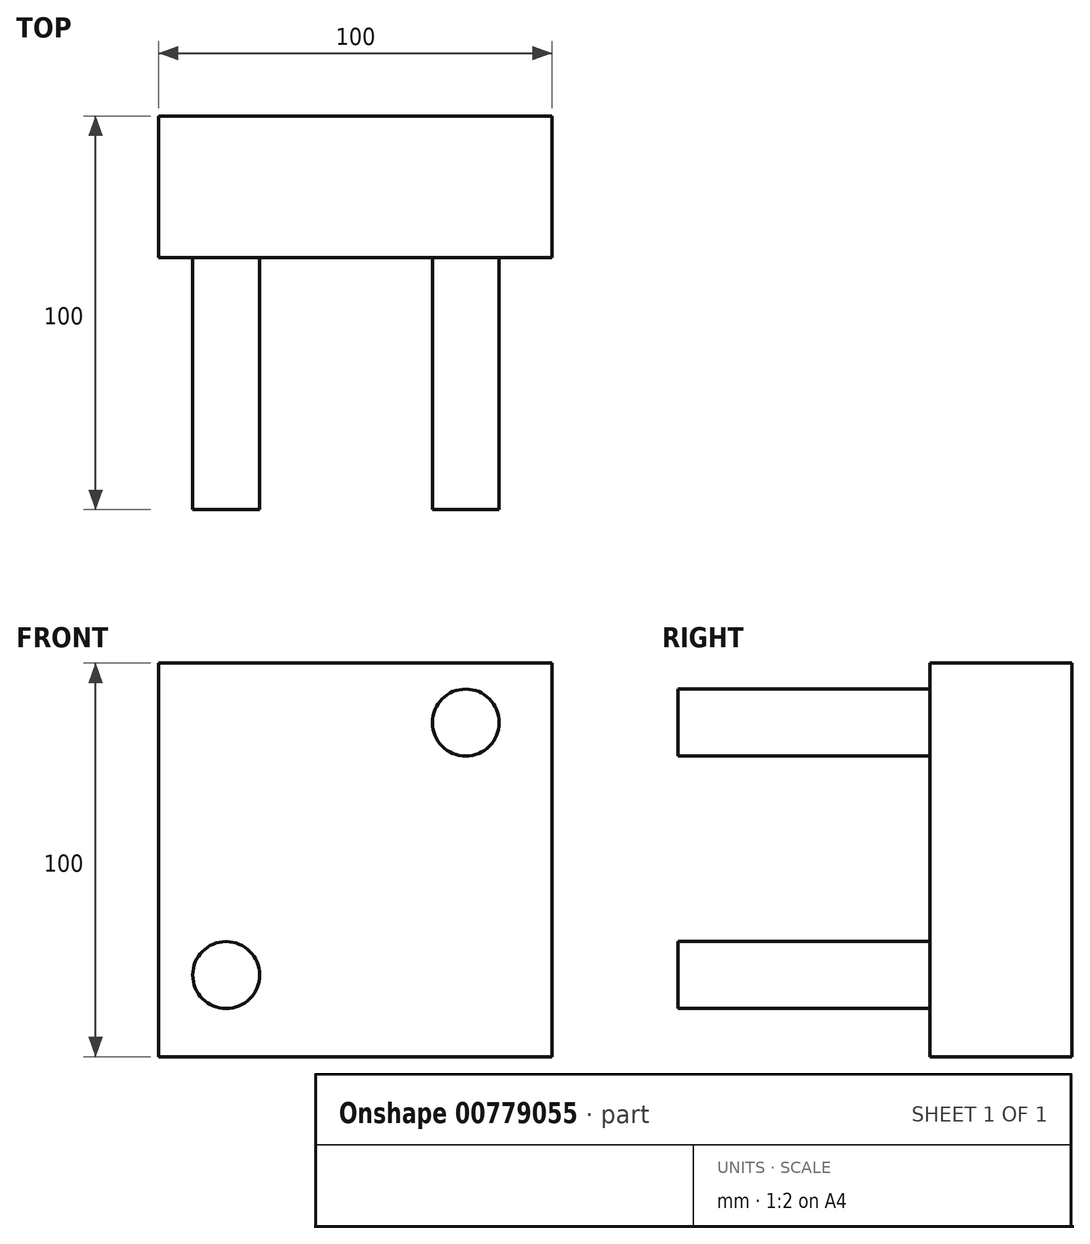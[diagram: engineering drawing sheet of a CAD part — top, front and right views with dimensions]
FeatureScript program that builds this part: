
annotation { "Feature Type Name" : "Feature", "Feature Type Description" : "" }
export const myFeature = defineFeature(function(context is Context, id is Id, definition is map)
    precondition{}
    {
        {
            var Q0;
            Q0=qCreatedBy(makeId("Front.planeOp"),FACE);
            var sketch = newSketch(context, id + "F0", { "sketchPlane" : qUnion([Q0])});
            skLineSegment(sketch, "E0.bottom", {"start": v(-47.6, 63.6) * mm, "end": v(52.4, 63.6) * mm});
            skLineSegment(sketch, "E0.top", {"start": v(-47.6, -36.4) * mm, "end": v(52.4, -36.4) * mm});
            skLineSegment(sketch, "E0.left", {"start": v(-47.6, 63.6) * mm, "end": v(-47.6, -36.4) * mm});
            skLineSegment(sketch, "E0.right", {"start": v(52.4, 63.6) * mm, "end": v(52.4, -36.4) * mm});
            skSolve(sketch);
        }
        {
            var Q0;
            Q0 = qSketchRegion(id + "F0", true);
            extrude(context, id + "F1", {"entities" : qUnion([Q0]), "depth" : 100 * mm, "offsetDistance" : 25 * mm});
        }
        {
            var Q0;
            Q0=makeQuery(id+"F1.opExtrude","CAP_FACE",FACE,{"disambiguationData":[OSD([sQuery(id+"F0.wireOp",EDGE,"E0.bottom"),sQuery(id+"F0.wireOp",EDGE,"E0.top"),sQuery(id+"F0.wireOp",EDGE,"E0.left"),sQuery(id+"F0.wireOp",EDGE,"E0.right")])],"isStart":false});
            var sketch = newSketch(context, id + "F2", { "sketchPlane" : qUnion([Q0])});
            skCircle(sketch, "E1", {"center": v(-30.44, 48.5) * mm, "radius": 8.5 * mm});
            skCircle(sketch, "E2.MirrorC", {"center": v(30.44, 48.5) * mm, "radius": 8.5 * mm});
            skCircle(sketch, "E3.MirrorC", {"center": v(-30.44, -15.65) * mm, "radius": 8.5 * mm});
            skCircle(sketch, "E4.MirrorC", {"center": v(30.44, -15.65) * mm, "radius": 8.5 * mm});
            skSolve(sketch);
        }
        {
            var Q0;
            Q0=makeQuery(id+"F2.imprint","IMPRINT",FACE,{"disambiguationData":[TD([[makeQuery(id+"F2.imprint","IMPRINT",EDGE,{"derivedFrom":sQuery(id+"F2.wireOp",EDGE,"E2.MirrorC")}),-1.0]])]});
            var Q1;
            Q1=makeQuery(id+"F2.imprint","IMPRINT",FACE,{"disambiguationData":[TD([[makeQuery(id+"F2.imprint","IMPRINT",EDGE,{"derivedFrom":sQuery(id+"F2.wireOp",EDGE,"E3.MirrorC")}),-1.0]])]});
            var Q2;
            Q2=makeQuery(id+"F2.imprint","IMPRINT",FACE,{"disambiguationData":[TD([[makeQuery(id+"F2.imprint","IMPRINT",EDGE,{"derivedFrom":sQuery(id+"F2.wireOp",EDGE,"E4.MirrorC")}),1.0]])]});
            var Q3;
            Q3=makeQuery(id+"F2.imprint","IMPRINT",FACE,{"disambiguationData":[TD([[makeQuery(id+"F2.imprint","IMPRINT",EDGE,{"derivedFrom":sQuery(id+"F2.wireOp",EDGE,"f4eeDJDL-5iWv-AFPj-o37r-ou3OiQOnMEaG")}),1.0]])]});
            var Q4;
            Q4=makeQuery(id+"F2.imprint","IMPRINT",FACE,{"disambiguationData":[TD([[makeQuery(id+"F2.imprint","IMPRINT",EDGE,{"derivedFrom":sQuery(id+"F2.wireOp",EDGE,"E1")}),1.0]])]});
            var Q5;
            Q5 = qSketchRegion(id + "F4", true);
            extrude(context, id + "F3", {"entities" : qUnion([Q0, Q1, Q2, Q3, Q4, Q5]), "operationType" : NewBodyOperationType.REMOVE, "oppositeDirection" : true, "depth" : 64 * mm, "offsetDistance" : 25 * mm});
        }
        {
            var Q0;
            Q0=makeQuery(id+"F1.opExtrude","CAP_FACE",FACE,{"disambiguationData":[OSD([sQuery(id+"F0.wireOp",EDGE,"E0.bottom"),sQuery(id+"F0.wireOp",EDGE,"E0.top"),sQuery(id+"F0.wireOp",EDGE,"E0.left"),sQuery(id+"F0.wireOp",EDGE,"E0.right")])],"isStart":false});
            var sketch = newSketch(context, id + "F4", { "sketchPlane" : qUnion([Q0])});
            skCircle(sketch, "E5", {"center": v(0, 13.41) * mm, "radius": 13.41 * mm});
            skLineSegment(sketch, "E6", {"start": v(0, 34.55) * mm, "end": v(0, -5.92) * mm});
            skSolve(sketch);
        }
        {
            var Q0;
            {var subQ0=sQuery(id+"F4.wireOp",EDGE,"E6");var subQ1=sQuery(id+"F4.wireOp",EDGE,"E5");var subQ2=makeQuery(id+"F4.imprint","INTERSECT",VERTEX,{"disambiguationData":[OD(0.0)],"derivedFrom":[subQ1,subQ0]});Q0=makeQuery(id+"F4.imprint","IMPRINT",FACE,{"disambiguationData":[TD([[makeQuery(id+"F4.imprint","IMPRINT",EDGE,{"disambiguationData":[TD([[subQ2,-1.0]])],"derivedFrom":subQ1}),1.0]])]});}
            var Q1;
            Q1=sQuery(id+"F4.wireOp",EDGE,"E6");
            revolve(context, id + "F5", {"operationType" : NewBodyOperationType.REMOVE, "surfaceOperationType" : NewSurfaceOperationType.NEW, "entities" : qUnion([Q0]), "axis" : qUnion([Q1]), "revolveType" : RevolveType.ONE_DIRECTION, "oppositeDirection" : true, "angle" : 180 * degree});
        }
    });
